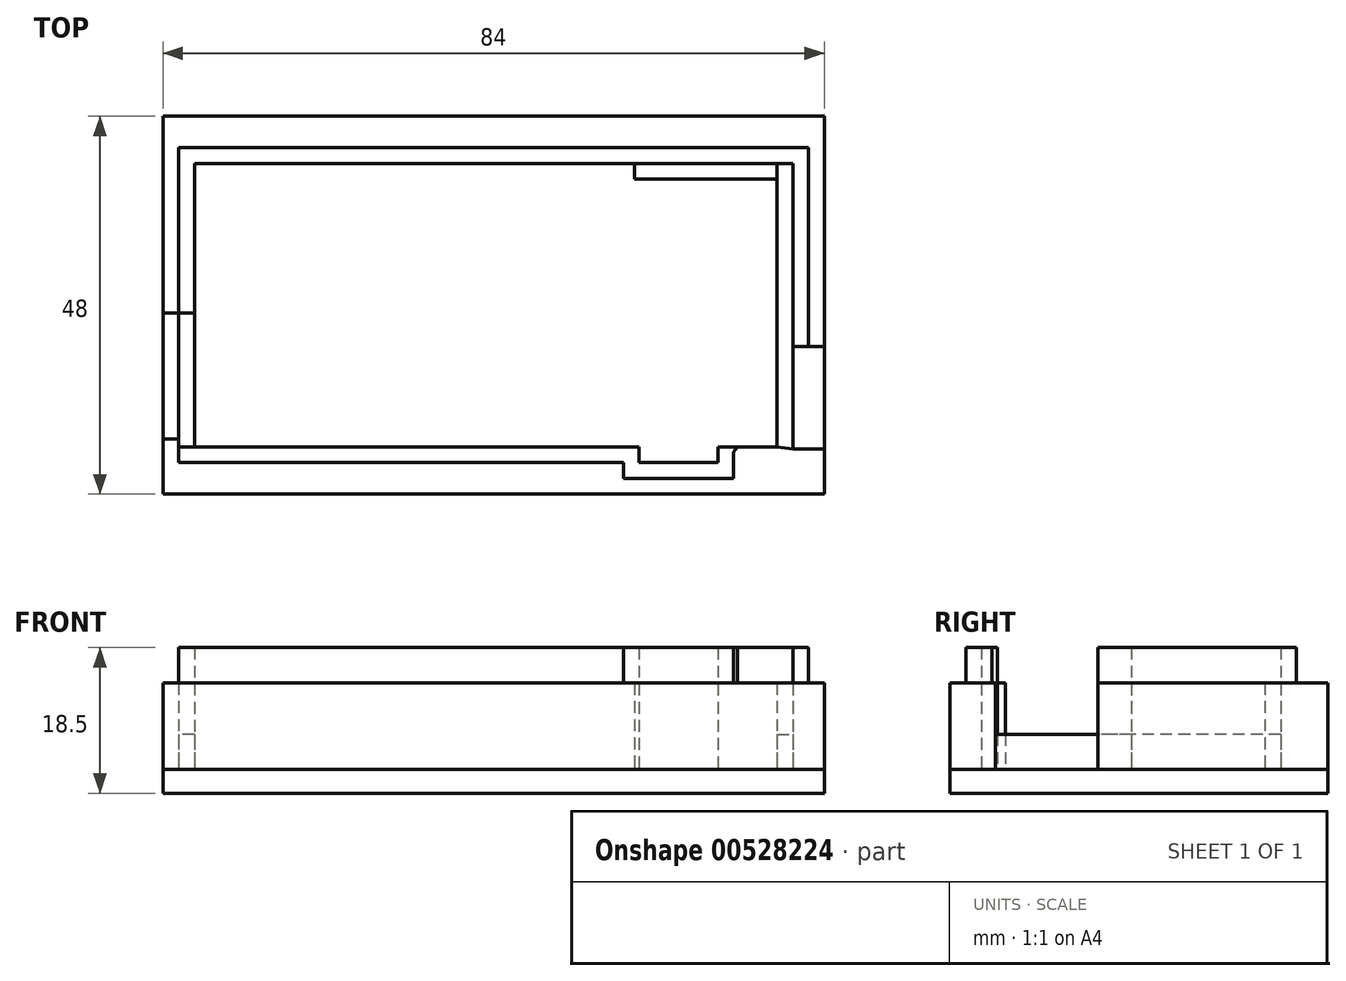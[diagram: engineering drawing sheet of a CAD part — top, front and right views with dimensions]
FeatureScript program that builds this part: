
annotation { "Feature Type Name" : "Feature", "Feature Type Description" : "" }
export const myFeature = defineFeature(function(context is Context, id is Id, definition is map)
    precondition{}
    {
        {
            var Q0;
            Q0=qCreatedBy(makeId("Top.planeOp"),FACE);
            var sketch = newSketch(context, id + "F0", { "sketchPlane" : qUnion([Q0])});
            skLineSegment(sketch, "E0.bottom", {"start": v(-48.88, 0.43) * mm, "end": v(29.12, 0.43) * mm});
            skLineSegment(sketch, "E0.left", {"start": v(-48.88, 0.43) * mm, "end": v(-48.88, -35.57) * mm});
            skLineSegment(sketch, "E1.0", {"start": v(-50.88, -41.57) * mm, "end": v(30.12, -41.57) * mm});
            skLineSegment(sketch, "E2.0", {"start": v(-50.88, 6.43) * mm, "end": v(30.12, 6.43) * mm});
            skLineSegment(sketch, "E3.0", {"start": v(-50.88, -1.57) * mm, "end": v(-50.88, -35.57) * mm});
            skLineSegment(sketch, "E4", {"start": v(-50.88, -1.57) * mm, "end": v(-50.88, 6.43) * mm});
            skLineSegment(sketch, "E5", {"start": v(-50.88, 6.43) * mm, "end": v(-50.88, 6.43) * mm});
            skLineSegment(sketch, "E6", {"start": v(-50.88, -41.57) * mm, "end": v(-50.88, -41.57) * mm});
            skLineSegment(sketch, "E7", {"start": v(-50.88, -35.57) * mm, "end": v(-50.88, -41.57) * mm});
            skLineSegment(sketch, "E8", {"start": v(29.12, 6.43) * mm, "end": v(29.12, -41.57) * mm});
            skLineSegment(sketch, "E9", {"start": v(30.12, -41.57) * mm, "end": v(33.12, -41.57) * mm});
            skLineSegment(sketch, "E10", {"start": v(30.12, 6.43) * mm, "end": v(33.12, 6.43) * mm});
            skLineSegment(sketch, "E11", {"start": v(33.12, 6.43) * mm, "end": v(33.12, -41.57) * mm});
            skLineSegment(sketch, "E12", {"start": v(-46.88, -35.57) * mm, "end": v(-46.88, 0.43) * mm});
            skLineSegment(sketch, "E13", {"start": v(-50.88, 6.43) * mm, "end": v(-50.88, -41.57) * mm});
            skLineSegment(sketch, "E14", {"start": v(9.62, -37.57) * mm, "end": v(19.62, -37.57) * mm});
            skLineSegment(sketch, "E15", {"start": v(19.62, -37.57) * mm, "end": v(19.62, -35.57) * mm});
            skLineSegment(sketch, "E16", {"start": v(9.62, -37.57) * mm, "end": v(9.62, -35.57) * mm});
            skLineSegment(sketch, "E17", {"start": v(29.12, -35.82) * mm, "end": v(33.12, -35.82) * mm});
            skLineSegment(sketch, "E18", {"start": v(29.12, -22.82) * mm, "end": v(33.12, -22.82) * mm});
            skLineSegment(sketch, "E19", {"start": v(31.12, 6.43) * mm, "end": v(31.12, -41.57) * mm});
            skLineSegment(sketch, "E20", {"start": v(29.12, 0.43) * mm, "end": v(33.12, 0.43) * mm});
            skLineSegment(sketch, "E21", {"start": v(9.62, -35.57) * mm, "end": v(-48.88, -35.57) * mm});
            skLineSegment(sketch, "E22", {"start": v(9.62, -35.57) * mm, "end": v(19.62, -35.57) * mm});
            skLineSegment(sketch, "E23", {"start": v(-46.88, -34.57) * mm, "end": v(-50.88, -34.57) * mm});
            skLineSegment(sketch, "E24", {"start": v(-50.88, -18.57) * mm, "end": v(-46.88, -18.57) * mm});
            skLineSegment(sketch, "E25", {"start": v(27.12, 0.43) * mm, "end": v(27.12, -35.57) * mm});
            skLineSegment(sketch, "E26", {"start": v(27.12, -1.57) * mm, "end": v(9.02, -1.57) * mm});
            skLineSegment(sketch, "E27", {"start": v(9.02, -1.57) * mm, "end": v(9.02, 0.43) * mm});
            skLineSegment(sketch, "E28", {"start": v(19.62, -35.57) * mm, "end": v(27.12, -35.57) * mm});
            skLineSegment(sketch, "E29", {"start": v(27.12, -35.57) * mm, "end": v(27.12, -41.57) * mm});
            skLineSegment(sketch, "E30", {"start": v(29.12, -35.82) * mm, "end": v(27.12, -35.57) * mm});
            skSolve(sketch);
        }
        {
            var Q0;
            {var subQ3=sQuery(id+"F0.wireOp",EDGE,"E12");Q0=makeQuery(id+"F0.imprint","IMPRINT",FACE,{"disambiguationData":[TD([[makeQuery(id+"F0.imprint","IMPRINT",EDGE,{"derivedFrom":subQ3}),-1.0]])]});}
            var Q1;
            Q1=makeQuery(id+"F0.imprint","IMPRINT",FACE,{"disambiguationData":[TD([[makeQuery(id+"F0.imprint","IMPRINT",EDGE,{"derivedFrom":sQuery(id+"F0.wireOp",EDGE,"E3.0")}),1.0]])]});
            var Q2;
            {var subQ6=sQuery(id+"F0.wireOp",EDGE,"E9");Q2=makeQuery(id+"F0.imprint","IMPRINT",FACE,{"disambiguationData":[TD([[makeQuery(id+"F0.imprint","IMPRINT",EDGE,{"derivedFrom":subQ6}),1.0]])]});}
            var Q3;
            {var subQ1=sQuery(id+"F0.wireOp",EDGE,"E0.top");var subQ5=sQuery(id+"F0.wireOp",EDGE,"E13");var subQ8=makeQuery(id+"F0.imprint","INTERSECT",VERTEX,{"derivedFrom":[subQ1,subQ5]});Q3=makeQuery(id+"F0.imprint","IMPRINT",FACE,{"disambiguationData":[TD([[makeQuery(id+"F0.imprint","IMPRINT",EDGE,{"disambiguationData":[TD([[subQ8,-1.0]])],"derivedFrom":subQ1}),-1.0]])]});}
            var Q4;
            {var subQ1=sQuery(id+"F0.wireOp",EDGE,"E0.bottom");var subQ5=sQuery(id+"F0.wireOp",EDGE,"E13");var subQ8=makeQuery(id+"F0.imprint","INTERSECT",VERTEX,{"derivedFrom":[subQ1,subQ5]});Q4=makeQuery(id+"F0.imprint","IMPRINT",FACE,{"disambiguationData":[TD([[makeQuery(id+"F0.imprint","IMPRINT",EDGE,{"disambiguationData":[TD([[subQ8,-1.0]])],"derivedFrom":subQ1}),1.0]])]});}
            var Q5;
            {var subQ3=sQuery(id+"F0.wireOp",EDGE,"E12");Q5=makeQuery(id+"F0.imprint","IMPRINT",FACE,{"disambiguationData":[TD([[makeQuery(id+"F0.imprint","IMPRINT",EDGE,{"derivedFrom":subQ3}),1.0]])]});}
            var Q6;
            {var subQ0=sQuery(id+"F0.wireOp",EDGE,"E10");Q6=makeQuery(id+"F0.imprint","IMPRINT",FACE,{"disambiguationData":[TD([[makeQuery(id+"F0.imprint","IMPRINT",EDGE,{"derivedFrom":subQ0}),-1.0]])]});}
            var Q7;
            {var subQ0=sQuery(id+"F0.wireOp",EDGE,"E17");Q7=makeQuery(id+"F0.imprint","IMPRINT",FACE,{"disambiguationData":[TD([[makeQuery(id+"F0.imprint","IMPRINT",EDGE,{"derivedFrom":subQ0}),1.0]])]});}
            var Q8;
            Q8=makeQuery(id+"F0.imprint","IMPRINT",FACE,{"disambiguationData":[TD([[makeQuery(id+"F0.imprint","IMPRINT",EDGE,{"derivedFrom":sQuery(id+"F0.wireOp",EDGE,"E14")}),1.0]])]});
            var Q9;
            {var subQ0=sQuery(id+"F0.wireOp",EDGE,"E9");var subQ1=sQuery(id+"F0.wireOp",EDGE,"E1.0");var subQ2=makeQuery(id+"F0.imprint","INTERSECT",VERTEX,{"derivedFrom":[subQ1,subQ0]});Q9=makeQuery(id+"F0.imprint","IMPRINT",FACE,{"disambiguationData":[TD([[makeQuery(id+"F0.imprint","IMPRINT",EDGE,{"disambiguationData":[TD([[subQ2,1.0]])],"derivedFrom":subQ1}),1.0]])]});}
            var Q10;
            {var subQ1=sQuery(id+"F0.wireOp",EDGE,"E8");var subQ3=sQuery(id+"F0.wireOp",EDGE,"E17");var subQ4=makeQuery(id+"F0.imprint","INTERSECT",VERTEX,{"derivedFrom":[subQ1,subQ3]});Q10=makeQuery(id+"F0.imprint","IMPRINT",FACE,{"disambiguationData":[TD([[makeQuery(id+"F0.imprint","IMPRINT",EDGE,{"disambiguationData":[TD([[subQ4,-1.0]])],"derivedFrom":subQ3}),-1.0]])]});}
            var Q11;
            {var subQ0=sQuery(id+"F0.wireOp",EDGE,"E17");var subQ1=sQuery(id+"F0.wireOp",EDGE,"E11");var subQ2=makeQuery(id+"F0.imprint","INTERSECT",VERTEX,{"derivedFrom":[subQ1,subQ0]});Q11=makeQuery(id+"F0.imprint","IMPRINT",FACE,{"disambiguationData":[TD([[makeQuery(id+"F0.imprint","IMPRINT",EDGE,{"disambiguationData":[TD([[subQ2,-1.0]])],"derivedFrom":subQ1}),-1.0]])]});}
            var Q12;
            {var subQ1=sQuery(id+"F0.wireOp",EDGE,"E8");var subQ3=sQuery(id+"F0.wireOp",EDGE,"E18");var subQ4=makeQuery(id+"F0.imprint","INTERSECT",VERTEX,{"derivedFrom":[subQ1,subQ3]});Q12=makeQuery(id+"F0.imprint","IMPRINT",FACE,{"disambiguationData":[TD([[makeQuery(id+"F0.imprint","IMPRINT",EDGE,{"disambiguationData":[TD([[subQ4,-1.0]])],"derivedFrom":subQ3}),1.0]])]});}
            var Q13;
            {var subQ0=sQuery(id+"F0.wireOp",EDGE,"E18");var subQ1=sQuery(id+"F0.wireOp",EDGE,"E11");var subQ2=makeQuery(id+"F0.imprint","INTERSECT",VERTEX,{"derivedFrom":[subQ1,subQ0]});Q13=makeQuery(id+"F0.imprint","IMPRINT",FACE,{"disambiguationData":[TD([[makeQuery(id+"F0.imprint","IMPRINT",EDGE,{"disambiguationData":[TD([[subQ2,1.0]])],"derivedFrom":subQ1}),-1.0]])]});}
            var Q14;
            {var subQ0=sQuery(id+"F0.wireOp",EDGE,"E10");var subQ1=sQuery(id+"F0.wireOp",EDGE,"E2.0");var subQ2=makeQuery(id+"F0.imprint","INTERSECT",VERTEX,{"derivedFrom":[subQ1,subQ0]});Q14=makeQuery(id+"F0.imprint","IMPRINT",FACE,{"disambiguationData":[TD([[makeQuery(id+"F0.imprint","IMPRINT",EDGE,{"disambiguationData":[TD([[subQ2,1.0]])],"derivedFrom":subQ1}),-1.0]])]});}
            var Q15;
            Q15=makeQuery(id+"F0.imprint","IMPRINT",FACE,{"disambiguationData":[TD([[makeQuery(id+"F0.imprint","IMPRINT",EDGE,{"derivedFrom":sQuery(id+"F0.wireOp",EDGE,"E14")}),-1.0]])]});
            var Q16;
            {var subQ3=sQuery(id+"F0.wireOp",EDGE,"E4");Q16=makeQuery(id+"F0.imprint","IMPRINT",FACE,{"disambiguationData":[TD([[makeQuery(id+"F0.imprint","IMPRINT",EDGE,{"derivedFrom":subQ3}),-1.0]])]});}
            var Q17;
            {var subQ2=sQuery(id+"F0.wireOp",EDGE,"E6");Q17=makeQuery(id+"F0.imprint","IMPRINT",FACE,{"disambiguationData":[TD([[makeQuery(id+"F0.imprint","IMPRINT",EDGE,{"derivedFrom":subQ2}),-1.0]])]});}
            var Q18;
            {var subQ6=sQuery(id+"F0.wireOp",EDGE,"E25");Q18=makeQuery(id+"F0.imprint","IMPRINT",FACE,{"disambiguationData":[TD([[makeQuery(id+"F0.imprint","IMPRINT",EDGE,{"derivedFrom":subQ6}),1.0]])]});}
            var Q19;
            {var subQ4=sQuery(id+"F0.wireOp",EDGE,"E26");Q19=makeQuery(id+"F0.imprint","IMPRINT",FACE,{"disambiguationData":[TD([[makeQuery(id+"F0.imprint","IMPRINT",EDGE,{"derivedFrom":subQ4}),-1.0]])]});}
            var Q20;
            {var subQ3=sQuery(id+"F0.wireOp",EDGE,"E29");Q20=makeQuery(id+"F0.imprint","IMPRINT",FACE,{"disambiguationData":[TD([[makeQuery(id+"F0.imprint","IMPRINT",EDGE,{"derivedFrom":subQ3}),1.0]])]});}
            extrude(context, id + "F1", {"entities" : qUnion([Q0, Q1, Q2, Q3, Q4, Q5, Q6, Q7, Q8, Q9, Q10, Q11, Q12, Q13, Q14, Q15, Q16, Q17, Q18, Q19, Q20]), "oppositeDirection" : true, "depth" : 3 * mm, "offsetDistance" : 25 * mm});
        }
        {
            var Q0;
            {var subQ0=sQuery(id+"F0.wireOp",EDGE,"E24");var subQ1=sQuery(id+"F0.wireOp",EDGE,"E0.left");var subQ2=makeQuery(id+"F0.imprint","INTERSECT",VERTEX,{"derivedFrom":[subQ1,subQ0]});Q0=makeQuery(id+"F0.imprint","IMPRINT",FACE,{"disambiguationData":[TD([[makeQuery(id+"F0.imprint","IMPRINT",EDGE,{"disambiguationData":[TD([[subQ2,-1.0]])],"derivedFrom":subQ1}),1.0]])]});}
            var Q1;
            {var subQ0=sQuery(id+"F0.wireOp",EDGE,"E21");var subQ1=sQuery(id+"F0.wireOp",EDGE,"E0.left");var subQ2=makeQuery(id+"F0.imprint","INTERSECT",VERTEX,{"derivedFrom":[subQ1,subQ0]});Q1=makeQuery(id+"F0.imprint","IMPRINT",FACE,{"disambiguationData":[TD([[makeQuery(id+"F0.imprint","IMPRINT",EDGE,{"disambiguationData":[TD([[subQ2,1.0]])],"derivedFrom":subQ1}),1.0]])]});}
            extrude(context, id + "F2", {"entities" : qUnion([Q0, Q1]), "operationType" : NewBodyOperationType.ADD, "depth" : 4.5 * mm, "offsetDistance" : 25 * mm});
        }
        {
            var Q0;
            {var subQ0=sQuery(id+"F0.wireOp",EDGE,"E18");var subQ1=sQuery(id+"F0.wireOp",EDGE,"E11");var subQ2=makeQuery(id+"F0.imprint","INTERSECT",VERTEX,{"derivedFrom":[subQ1,subQ0]});Q0=makeQuery(id+"F0.imprint","IMPRINT",FACE,{"disambiguationData":[TD([[makeQuery(id+"F0.imprint","IMPRINT",EDGE,{"disambiguationData":[TD([[subQ2,1.0]])],"derivedFrom":subQ1}),-1.0]])]});}
            var Q1;
            {var subQ1=sQuery(id+"F0.wireOp",EDGE,"E8");var subQ3=sQuery(id+"F0.wireOp",EDGE,"E18");var subQ4=makeQuery(id+"F0.imprint","INTERSECT",VERTEX,{"derivedFrom":[subQ1,subQ3]});Q1=makeQuery(id+"F0.imprint","IMPRINT",FACE,{"disambiguationData":[TD([[makeQuery(id+"F0.imprint","IMPRINT",EDGE,{"disambiguationData":[TD([[subQ4,-1.0]])],"derivedFrom":subQ3}),1.0]])]});}
            var Q2;
            {var subQ0=sQuery(id+"F0.wireOp",EDGE,"E10");var subQ1=sQuery(id+"F0.wireOp",EDGE,"E2.0");var subQ2=makeQuery(id+"F0.imprint","INTERSECT",VERTEX,{"derivedFrom":[subQ1,subQ0]});Q2=makeQuery(id+"F0.imprint","IMPRINT",FACE,{"disambiguationData":[TD([[makeQuery(id+"F0.imprint","IMPRINT",EDGE,{"disambiguationData":[TD([[subQ2,1.0]])],"derivedFrom":subQ1}),-1.0]])]});}
            var Q3;
            {var subQ1=sQuery(id+"F0.wireOp",EDGE,"E8");var subQ3=sQuery(id+"F0.wireOp",EDGE,"E17");var subQ4=makeQuery(id+"F0.imprint","INTERSECT",VERTEX,{"derivedFrom":[subQ1,subQ3]});Q3=makeQuery(id+"F0.imprint","IMPRINT",FACE,{"disambiguationData":[TD([[makeQuery(id+"F0.imprint","IMPRINT",EDGE,{"disambiguationData":[TD([[subQ4,-1.0]])],"derivedFrom":subQ3}),-1.0]])]});}
            var Q4;
            {var subQ0=sQuery(id+"F0.wireOp",EDGE,"E11");var subQ1=sQuery(id+"F0.wireOp",EDGE,"E9");var subQ2=makeQuery(id+"F0.imprint","INTERSECT",VERTEX,{"derivedFrom":[subQ1,subQ0]});Q4=makeQuery(id+"F0.imprint","IMPRINT",FACE,{"disambiguationData":[TD([[makeQuery(id+"F0.imprint","IMPRINT",EDGE,{"disambiguationData":[TD([[subQ2,1.0]])],"derivedFrom":subQ1}),1.0]])]});}
            var Q5;
            {var subQ0=sQuery(id+"F0.wireOp",EDGE,"E17");var subQ1=sQuery(id+"F0.wireOp",EDGE,"E11");var subQ2=makeQuery(id+"F0.imprint","INTERSECT",VERTEX,{"derivedFrom":[subQ1,subQ0]});Q5=makeQuery(id+"F0.imprint","IMPRINT",FACE,{"disambiguationData":[TD([[makeQuery(id+"F0.imprint","IMPRINT",EDGE,{"disambiguationData":[TD([[subQ2,-1.0]])],"derivedFrom":subQ1}),-1.0]])]});}
            var Q6;
            {var subQ0=sQuery(id+"F0.wireOp",EDGE,"E9");var subQ1=sQuery(id+"F0.wireOp",EDGE,"E1.0");var subQ2=makeQuery(id+"F0.imprint","INTERSECT",VERTEX,{"derivedFrom":[subQ1,subQ0]});Q6=makeQuery(id+"F0.imprint","IMPRINT",FACE,{"disambiguationData":[TD([[makeQuery(id+"F0.imprint","IMPRINT",EDGE,{"disambiguationData":[TD([[subQ2,1.0]])],"derivedFrom":subQ1}),1.0]])]});}
            var Q7;
            {var subQ0=sQuery(id+"F0.wireOp",EDGE,"E11");var subQ1=sQuery(id+"F0.wireOp",EDGE,"E10");var subQ2=makeQuery(id+"F0.imprint","INTERSECT",VERTEX,{"derivedFrom":[subQ1,subQ0]});Q7=makeQuery(id+"F0.imprint","IMPRINT",FACE,{"disambiguationData":[TD([[makeQuery(id+"F0.imprint","IMPRINT",EDGE,{"disambiguationData":[TD([[subQ2,1.0]])],"derivedFrom":subQ1}),-1.0]])]});}
            var Q8;
            {var subQ0=sQuery(id+"F0.wireOp",EDGE,"E13");var subQ5=sQuery(id+"F0.wireOp",EDGE,"E0.bottom");var subQ6=makeQuery(id+"F0.imprint","INTERSECT",VERTEX,{"derivedFrom":[subQ5,subQ0]});Q8=makeQuery(id+"F0.imprint","IMPRINT",FACE,{"disambiguationData":[TD([[makeQuery(id+"F0.imprint","IMPRINT",EDGE,{"disambiguationData":[TD([[subQ6,-1.0]])],"derivedFrom":subQ5}),1.0]])]});}
            var Q9;
            Q9=makeQuery(id+"F0.imprint","IMPRINT",FACE,{"disambiguationData":[TD([[makeQuery(id+"F0.imprint","IMPRINT",EDGE,{"derivedFrom":sQuery(id+"F0.wireOp",EDGE,"E14")}),-1.0]])]});
            var Q10;
            {var subQ2=sQuery(id+"F0.wireOp",EDGE,"E6");Q10=makeQuery(id+"F0.imprint","IMPRINT",FACE,{"disambiguationData":[TD([[makeQuery(id+"F0.imprint","IMPRINT",EDGE,{"derivedFrom":subQ2}),-1.0]])]});}
            var Q11;
            {var subQ3=sQuery(id+"F0.wireOp",EDGE,"E4");Q11=makeQuery(id+"F0.imprint","IMPRINT",FACE,{"disambiguationData":[TD([[makeQuery(id+"F0.imprint","IMPRINT",EDGE,{"derivedFrom":subQ3}),-1.0]])]});}
            var Q12;
            {var subQ0=sQuery(id+"F0.wireOp",EDGE,"E13");var subQ1=sQuery(id+"F0.wireOp",EDGE,"E0.bottom");var subQ2=makeQuery(id+"F0.imprint","INTERSECT",VERTEX,{"derivedFrom":[subQ1,subQ0]});Q12=makeQuery(id+"F0.imprint","IMPRINT",FACE,{"disambiguationData":[TD([[makeQuery(id+"F0.imprint","IMPRINT",EDGE,{"disambiguationData":[TD([[subQ2,-1.0]])],"derivedFrom":subQ1}),-1.0]])]});}
            var Q13;
            {var subQ3=sQuery(id+"F0.wireOp",EDGE,"E29");Q13=makeQuery(id+"F0.imprint","IMPRINT",FACE,{"disambiguationData":[TD([[makeQuery(id+"F0.imprint","IMPRINT",EDGE,{"derivedFrom":subQ3}),1.0]])]});}
            extrude(context, id + "F3", {"entities" : qUnion([Q0, Q1, Q2, Q3, Q4, Q5, Q6, Q7, Q8, Q9, Q10, Q11, Q12, Q13]), "depth" : 11 * mm, "offsetDistance" : 25 * mm});
        }
        {
            var Q0;
            Q0=makeQuery(id+"F3.opExtrude","CAP_FACE",FACE,{"disambiguationData":[OSD([sQuery(id+"F0.wireOp",EDGE,"E0.bottom"),sQuery(id+"F0.wireOp",EDGE,"E1.0"),sQuery(id+"F0.wireOp",EDGE,"E2.0"),sQuery(id+"F0.wireOp",EDGE,"E3.0"),sQuery(id+"F0.wireOp",EDGE,"E4"),sQuery(id+"F0.wireOp",EDGE,"E5"),sQuery(id+"F0.wireOp",EDGE,"E6"),sQuery(id+"F0.wireOp",EDGE,"E7"),sQuery(id+"F0.wireOp",EDGE,"E8"),sQuery(id+"F0.wireOp",EDGE,"E9"),sQuery(id+"F0.wireOp",EDGE,"E10"),sQuery(id+"F0.wireOp",EDGE,"E11"),sQuery(id+"F0.wireOp",EDGE,"E12"),sQuery(id+"F0.wireOp",EDGE,"E13"),sQuery(id+"F0.wireOp",EDGE,"E14"),sQuery(id+"F0.wireOp",EDGE,"E15"),sQuery(id+"F0.wireOp",EDGE,"E16"),sQuery(id+"F0.wireOp",EDGE,"E17"),sQuery(id+"F0.wireOp",EDGE,"E18"),sQuery(id+"F0.wireOp",EDGE,"E19"),sQuery(id+"F0.wireOp",EDGE,"svHIiPPS-1IlF-Ibmd-P32e-zllCd6fonRKQ"),sQuery(id+"F0.wireOp",EDGE,"E21"),sQuery(id+"F0.wireOp",EDGE,"E23"),sQuery(id+"F0.wireOp",EDGE,"E24")])],"isStart":false});
            var sketch = newSketch(context, id + "F4", { "sketchPlane" : qUnion([Q0])});
            skLineSegment(sketch, "E31", {"start": v(-50.88, 6.43) * mm, "end": v(33.12, 6.43) * mm});
            skLineSegment(sketch, "E32", {"start": v(33.12, -41.57) * mm, "end": v(-50.88, -41.57) * mm});
            skLineSegment(sketch, "E33", {"start": v(-50.88, -41.57) * mm, "end": v(-50.88, -34.57) * mm});
            skLineSegment(sketch, "E34", {"start": v(-50.88, -34.57) * mm, "end": v(-50.88, -34.57) * mm});
            skLineSegment(sketch, "E35", {"start": v(-48.88, -35.57) * mm, "end": v(9.62, -35.57) * mm});
            skLineSegment(sketch, "E36", {"start": v(9.62, -35.57) * mm, "end": v(9.62, -37.57) * mm});
            skLineSegment(sketch, "E37", {"start": v(9.62, -37.57) * mm, "end": v(19.62, -37.57) * mm});
            skLineSegment(sketch, "E38", {"start": v(19.62, -37.57) * mm, "end": v(19.62, -35.57) * mm});
            skLineSegment(sketch, "E39", {"start": v(19.62, -35.57) * mm, "end": v(29.12, -22.82) * mm});
            skLineSegment(sketch, "E40", {"start": v(29.12, -35.82) * mm, "end": v(29.12, -22.82) * mm});
            skLineSegment(sketch, "E41", {"start": v(29.12, -35.82) * mm, "end": v(33.12, -35.82) * mm});
            skLineSegment(sketch, "E42", {"start": v(29.12, -22.82) * mm, "end": v(29.12, -22.82) * mm});
            skLineSegment(sketch, "E43", {"start": v(29.12, -22.82) * mm, "end": v(29.12, 0.43) * mm});
            skLineSegment(sketch, "E44", {"start": v(29.12, 0.43) * mm, "end": v(-46.88, 0.43) * mm});
            skLineSegment(sketch, "E45", {"start": v(-46.88, 0.43) * mm, "end": v(-46.88, -18.57) * mm});
            skLineSegment(sketch, "E46", {"start": v(-46.88, -18.57) * mm, "end": v(-50.88, -18.57) * mm});
            skLineSegment(sketch, "E47", {"start": v(-50.88, -18.57) * mm, "end": v(-50.88, 6.43) * mm});
            skLineSegment(sketch, "E48.0", {"start": v(-48.88, 2.43) * mm, "end": v(-48.88, -18.57) * mm});
            skLineSegment(sketch, "E48.1", {"start": v(29.12, 2.43) * mm, "end": v(-48.88, 2.43) * mm});
            skLineSegment(sketch, "E49.0", {"start": v(31.12, -22.82) * mm, "end": v(31.12, 13.68) * mm});
            skLineSegment(sketch, "E50.0", {"start": v(21.62, -36.24) * mm, "end": v(30.87, -23.82) * mm});
            skLineSegment(sketch, "E50.2", {"start": v(7.62, -37.57) * mm, "end": v(7.62, -39.57) * mm});
            skLineSegment(sketch, "E50.3", {"start": v(7.62, -39.57) * mm, "end": v(21.62, -39.57) * mm});
            skLineSegment(sketch, "E50.4", {"start": v(21.62, -39.57) * mm, "end": v(21.62, -36.24) * mm});
            skLineSegment(sketch, "E51", {"start": v(30.87, -23.82) * mm, "end": v(32.94, -23.82) * mm});
            skLineSegment(sketch, "E52", {"start": v(29.12, 2.43) * mm, "end": v(31.12, 2.43) * mm});
            skLineSegment(sketch, "E53", {"start": v(31.12, 13.68) * mm, "end": v(31.12, 2.43) * mm});
            skLineSegment(sketch, "E54", {"start": v(-48.88, -35.57) * mm, "end": v(-48.88, -37.57) * mm});
            skLineSegment(sketch, "E55", {"start": v(-48.88, -37.57) * mm, "end": v(7.62, -37.57) * mm});
            skLineSegment(sketch, "E56", {"start": v(31.12, -22.82) * mm, "end": v(29.12, -22.82) * mm});
            skLineSegment(sketch, "E57", {"start": v(32.94, -35.82) * mm, "end": v(32.94, -23.82) * mm});
            skLineSegment(sketch, "E58", {"start": v(-48.88, -35.57) * mm, "end": v(-48.88, -34.57) * mm});
            skLineSegment(sketch, "E59", {"start": v(-48.88, -34.57) * mm, "end": v(-50.88, -34.57) * mm});
            skSolve(sketch);
        }
        {
            var Q0;
            Q0=makeQuery(id+"F4.imprint","IMPRINT",FACE,{"disambiguationData":[TD([[makeQuery(id+"F4.imprint","IMPRINT",EDGE,{"derivedFrom":sQuery(id+"F4.wireOp",EDGE,"E35")}),1.0]])]});
            var Q1;
            Q1=makeQuery(id+"F4.imprint","IMPRINT",FACE,{"disambiguationData":[TD([[makeQuery(id+"F4.imprint","IMPRINT",EDGE,{"derivedFrom":sQuery(id+"F4.wireOp",EDGE,"E42")}),1.0]])]});
            extrude(context, id + "F5", {"entities" : qUnion([Q0, Q1]), "operationType" : NewBodyOperationType.ADD, "depth" : 4.5 * mm, "offsetDistance" : 25 * mm});
        }
        {
            var Q0;
            {var subQ6=sQuery(id+"F0.wireOp",EDGE,"E25");Q0=makeQuery(id+"F0.imprint","IMPRINT",FACE,{"disambiguationData":[TD([[makeQuery(id+"F0.imprint","IMPRINT",EDGE,{"derivedFrom":subQ6}),1.0]])]});}
            extrude(context, id + "F6", {"entities" : qUnion([Q0]), "depth" : 4.5 * mm, "offsetDistance" : 25 * mm});
        }
        {
            var Q0;
            Q0=makeQuery(id+"F4.imprint","IMPRINT",FACE,{"disambiguationData":[TD([[makeQuery(id+"F4.imprint","IMPRINT",EDGE,{"derivedFrom":sQuery(id+"F4.wireOp",EDGE,"E43")}),-1.0]])]});
            extrude(context, id + "F7", {"entities" : qUnion([Q0]), "operationType" : NewBodyOperationType.ADD, "depth" : 4.5 * mm, "offsetDistance" : 25 * mm});
        }
    });
